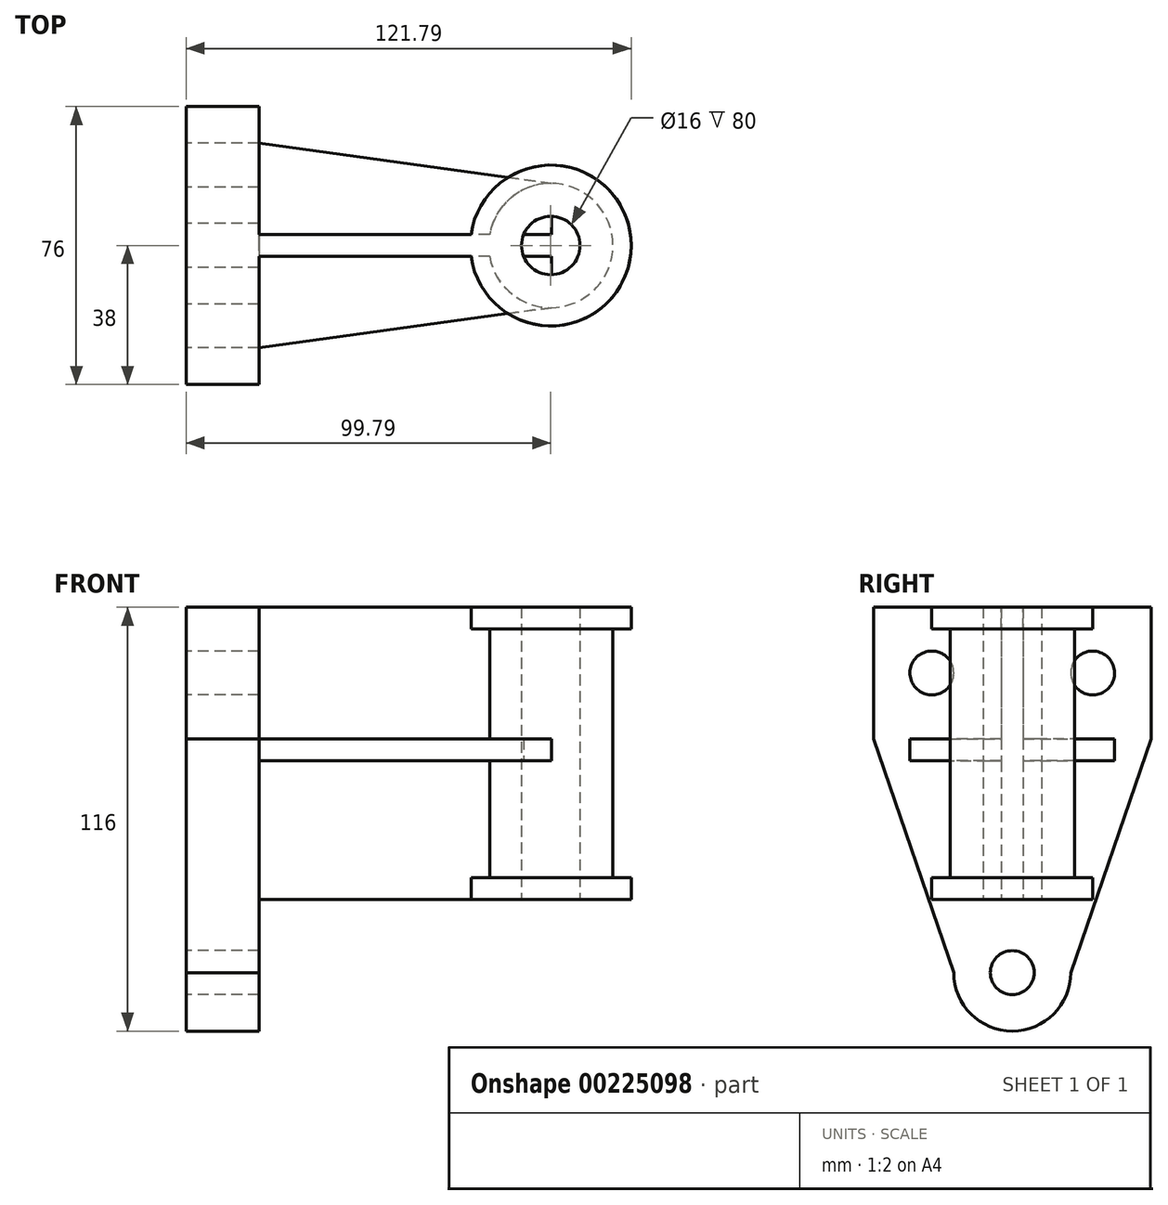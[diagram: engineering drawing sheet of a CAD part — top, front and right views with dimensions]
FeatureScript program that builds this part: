
annotation { "Feature Type Name" : "Feature", "Feature Type Description" : "" }
export const myFeature = defineFeature(function(context is Context, id is Id, definition is map)
    precondition{}
    {
        {
            var Q0;
            Q0=qCreatedBy(makeId("Top.planeOp"),FACE);
            var sketch = newSketch(context, id + "F0", { "sketchPlane" : qUnion([Q0])});
            skCircle(sketch, "E0", {"center": v(0, 0) * mm, "radius": 22 * mm});
            skCircle(sketch, "E1", {"center": v(0, 0) * mm, "radius": 17 * mm});
            skCircle(sketch, "E2", {"center": v(0, 0) * mm, "radius": 8 * mm});
            skSolve(sketch);
        }
        {
            var Q0;
            Q0=makeQuery(id+"F0.imprint","IMPRINT",FACE,{"disambiguationData":[TD([[makeQuery(id+"F0.imprint","IMPRINT",EDGE,{"derivedFrom":sQuery(id+"F0.wireOp",EDGE,"E0")}),1.0]])]});
            extrude(context, id + "F1", {"entities" : qUnion([Q0]), "depth" : 6 * mm});
        }
        {
            var Q0;
            Q0=makeQuery(id+"F0.imprint","IMPRINT",FACE,{"disambiguationData":[TD([[makeQuery(id+"F0.imprint","IMPRINT",EDGE,{"derivedFrom":sQuery(id+"F0.wireOp",EDGE,"E1")}),1.0]])]});
            extrude(context, id + "F2", {"entities" : qUnion([Q0]), "operationType" : NewBodyOperationType.ADD, "depth" : 40 * mm});
        }
        {
            var Q0;
            Q0=makeQuery(id+"F1.opExtrude","SWEPT_BODY",BODY,{"disambiguationData":[OSD([sQuery(id+"F0.wireOp",EDGE,"E0"),sQuery(id+"F0.wireOp",EDGE,"E1")])]});
            var Q1;
            Q1=makeQuery(id+"F2.opExtrude","CAP_FACE",FACE,{"disambiguationData":[OSD([sQuery(id+"F0.wireOp",EDGE,"E1"),sQuery(id+"F0.wireOp",EDGE,"E2")])],"isStart":false});
            mirror(context, id + "F3", {"entities" : qUnion([Q0]), "mirrorPlane" : qUnion([Q1])});
        }
        {
            var Q0;
            Q0=qCreatedBy(makeId("Top.planeOp"),FACE);
            var sketch = newSketch(context, id + "F4", { "sketchPlane" : qUnion([Q0])});
            skLineSegment(sketch, "E3", {"start": v(37.48, 0) * mm, "end": v(-105.07, 0) * mm, "construction": true});
            skLineSegment(sketch, "E4", {"start": v(-21.8, 3) * mm, "end": v(-99.8, 3) * mm});
            skLineSegment(sketch, "E5", {"start": v(-99.8, 3) * mm, "end": v(-99.8, -3) * mm});
            skLineSegment(sketch, "E6", {"start": v(-99.8, -3) * mm, "end": v(-21.8, -3) * mm});
            skLineSegment(sketch, "E7", {"start": v(-21.8, 3) * mm, "end": v(-16.73, 3) * mm});
            skLineSegment(sketch, "E8", {"start": v(-16.73, 3) * mm, "end": v(-16.73, -3) * mm});
            skLineSegment(sketch, "E9", {"start": v(-16.73, -3) * mm, "end": v(-21.8, -3) * mm});
            skSolve(sketch);
        }
        {
            var Q0;
            Q0=makeQuery(id+"F1.opExtrude","SWEPT_BODY",BODY,{"disambiguationData":[OSD([sQuery(id+"F0.wireOp",EDGE,"E0"),sQuery(id+"F0.wireOp",EDGE,"E1")])]});
            var Q1;
            Q1=makeQuery(id+"F3.opPattern","COPY",BODY,{"derivedFrom":makeQuery(id+"F1.opExtrude","SWEPT_BODY",BODY,{"disambiguationData":[OSD([sQuery(id+"F0.wireOp",EDGE,"E0"),sQuery(id+"F0.wireOp",EDGE,"E1")])]}),"instanceName":"1"});
            booleanBodies(context, id + "F5", {"operationType" : BooleanOperationType.UNION, "tools" : qUnion([Q0, Q1])});
        }
        {
            var Q0;
            Q0=makeQuery(id+"F4.imprint","IMPRINT",FACE,{"disambiguationData":[TD([[makeQuery(id+"F4.imprint","IMPRINT",EDGE,{"derivedFrom":sQuery(id+"F4.wireOp",EDGE,"E4")}),1.0]])]});
            var Q1;
            {var subQ0=sQuery(id+"F0.wireOp",EDGE,"E1");Q1=makeQuery(id+"F3.opPattern","COPY",FACE,{"derivedFrom":makeQuery(id+"F2.boolean.opBoolean","MERGE",FACE,{"derivedFrom":[makeQuery(id+"F1.opExtrude","CAP_FACE",FACE,{"disambiguationData":[OSD([sQuery(id+"F0.wireOp",EDGE,"E0"),subQ0])],"isStart":true}),makeQuery(id+"F2.opExtrude","CAP_FACE",FACE,{"disambiguationData":[OSD([subQ0,sQuery(id+"F0.wireOp",EDGE,"E2")])],"isStart":true})]}),"instanceName":"1"});}
            extrude(context, id + "F6", {"entities" : qUnion([Q0]), "operationType" : NewBodyOperationType.ADD, "endBound" : BoundingType.UP_TO_SURFACE, "endBoundEntityFace" : qUnion([Q1]), "depth" : 25 * mm});
        }
        {
            var Q0;
            Q0=makeQuery(id+"F6.opExtrude","SWEPT_FACE",FACE,{"disambiguationData":[OSD([sQuery(id+"F4.wireOp",EDGE,"E5")])]});
            var sketch = newSketch(context, id + "F7", { "sketchPlane" : qUnion([Q0])});
            skLineSegment(sketch, "E10", {"start": v(0, 102.74) * mm, "end": v(0, -20) * mm, "construction": true});
            skLineSegment(sketch, "E11", {"start": v(0, 80) * mm, "end": v(38, 80) * mm});
            skPoint(sketch, "E11.endSnap0", {"position": v(0, 80) * mm});
            skLineSegment(sketch, "E12", {"start": v(38, 80) * mm, "end": v(38, 44) * mm});
            skLineSegment(sketch, "E13", {"start": v(0, 80) * mm, "end": v(-38, 80) * mm});
            skLineSegment(sketch, "E14", {"start": v(-38, 80) * mm, "end": v(-38, 44) * mm});
            skLineSegment(sketch, "E15", {"start": v(-56.56, 62) * mm, "end": v(67.41, 62) * mm, "construction": true});
            skLineSegment(sketch, "E16", {"start": v(-84.06, -20) * mm, "end": v(98, -20) * mm, "construction": true});
            skCircle(sketch, "E17", {"center": v(0, -20) * mm, "radius": 6 * mm});
            skArc(sketch, "E18", {"start": v(-16, -20) * mm, "mid": v(0, -36) * mm, "end": v(16, -20) * mm});
            skLineSegment(sketch, "E19", {"start": v(-16, -20) * mm, "end": v(-38, 44) * mm});
            skLineSegment(sketch, "E20", {"start": v(16, -20) * mm, "end": v(38, 44) * mm});
            skCircle(sketch, "E21", {"center": v(-22, 62) * mm, "radius": 6 * mm});
            skCircle(sketch, "E22", {"center": v(22, 62) * mm, "radius": 6 * mm});
            skLineSegment(sketch, "E23", {"start": v(-28, 44) * mm, "end": v(28, 44) * mm});
            skLineSegment(sketch, "E24", {"start": v(28, 44) * mm, "end": v(28, 38) * mm});
            skLineSegment(sketch, "E25", {"start": v(28, 38) * mm, "end": v(-28, 38) * mm});
            skLineSegment(sketch, "E26", {"start": v(-28, 38) * mm, "end": v(-28, 44) * mm});
            skSolve(sketch);
        }
        {
            var Q0;
            {var subQ9=sQuery(id+"F7.wireOp",EDGE,"E12");Q0=makeQuery(id+"F7.imprint","IMPRINT",FACE,{"disambiguationData":[TD([[makeQuery(id+"F7.imprint","IMPRINT",EDGE,{"derivedFrom":subQ9}),-1.0]])]});}
            extrude(context, id + "F8", {"entities" : qUnion([Q0]), "operationType" : NewBodyOperationType.ADD, "oppositeDirection" : true, "depth" : 20 * mm});
        }
        {
            var Q0;
            {var subQ0=sQuery(id+"F4.wireOp",EDGE,"E5");Q0=makeQuery(id+"F8.boolean.opBoolean","MERGE",FACE,{"derivedFrom":[makeQuery(id+"F6.opExtrude","SWEPT_FACE",FACE,{"disambiguationData":[OSD([subQ0])]}),makeQuery(id+"F8.opExtrude","CAP_FACE",FACE,{"disambiguationData":[OSD([sQuery(id+"F4.wireOp",EDGE,"E4"),subQ0,sQuery(id+"F4.wireOp",EDGE,"E6"),sQuery(id+"F7.wireOp",EDGE,"E11"),sQuery(id+"F7.wireOp",EDGE,"E12"),sQuery(id+"F7.wireOp",EDGE,"E13"),sQuery(id+"F7.wireOp",EDGE,"E14"),sQuery(id+"F7.wireOp",EDGE,"E17"),sQuery(id+"F7.wireOp",EDGE,"E18"),sQuery(id+"F7.wireOp",EDGE,"E19"),sQuery(id+"F7.wireOp",EDGE,"E20"),sQuery(id+"F7.wireOp",EDGE,"E21"),sQuery(id+"F7.wireOp",EDGE,"E22")])],"isStart":true})]});}
            var sketch = newSketch(context, id + "F9", { "sketchPlane" : qUnion([Q0])});
            skSolve(sketch);
        }
        {
            var Q0;
            {var subQ0=sQuery(id+"F7.wireOp",EDGE,"E26");Q0=makeQuery(id+"F9.imprint","IMPRINT",FACE,{"disambiguationData":[TD([[makeQuery(id+"F9.imprint","IMPRINT",EDGE,{"derivedFrom":makeQuery(id+"F8.opExtrude","CAP_EDGE",EDGE,{"disambiguationData":[OSD([subQ0])],"isStart":true})}),-1.0]])]});}
            var Q1;
            {var subQ0=sQuery(id+"F7.wireOp",EDGE,"E24");Q1=makeQuery(id+"F9.imprint","IMPRINT",FACE,{"disambiguationData":[TD([[makeQuery(id+"F9.imprint","IMPRINT",EDGE,{"derivedFrom":makeQuery(id+"F8.opExtrude","CAP_EDGE",EDGE,{"disambiguationData":[OSD([subQ0])],"isStart":true})}),-1.0]])]});}
            extrude(context, id + "F10", {"entities" : qUnion([Q0, Q1]), "operationType" : NewBodyOperationType.ADD, "oppositeDirection" : true, "depth" : 100 * mm});
        }
        {
            var Q0;
            {var subQ2=sQuery(id+"F7.wireOp",EDGE,"E24");var subQ3=sQuery(id+"F7.wireOp",EDGE,"E23");var subQ5=makeQuery(id+"F2.opExtrude","SWEPT_FACE",FACE,{"disambiguationData":[OSD([sQuery(id+"F0.wireOp",EDGE,"E1")])]});Q0=makeQuery(id+"F10.boolean.opBoolean","SPLIT",FACE,{"disambiguationData":[TD([subQ5])],"derivedFrom":makeQuery(id+"F10.opExtrude","SWEPT_FACE",FACE,{"disambiguationData":[OSD([subQ3]),TDD([makeQuery(id+"F9.imprint","IMPRINT",EDGE,{"derivedFrom":makeQuery(id+"F8.opExtrude","CAP_EDGE",EDGE,{"disambiguationData":[OSD([subQ3]),TDD([makeQuery(id+"F7.imprint","IMPRINT",EDGE,{"disambiguationData":[TD([[makeQuery(id+"F7.imprint","INTERSECT",VERTEX,{"derivedFrom":[subQ3,subQ2]}),1.0]])],"derivedFrom":subQ3})])],"isStart":true})})])]})});}
            var sketch = newSketch(context, id + "F11", { "sketchPlane" : qUnion([Q0])});
            skLineSegment(sketch, "E27", {"start": v(-79.8, -28) * mm, "end": v(0.2, -17) * mm});
            skLineSegment(sketch, "E28", {"start": v(0.2, -17) * mm, "end": v(0.2, -28) * mm});
            skLineSegment(sketch, "E29", {"start": v(0.2, -28) * mm, "end": v(-79.8, -28) * mm});
            skSolve(sketch);
        }
        {
            var Q0;
            Q0=makeQuery(id+"F11.imprint","IMPRINT",FACE,{"disambiguationData":[TD([[makeQuery(id+"F11.imprint","IMPRINT",EDGE,{"derivedFrom":sQuery(id+"F11.wireOp",EDGE,"E27")}),-1.0]])]});
            extrude(context, id + "F12", {"entities" : qUnion([Q0]), "operationType" : NewBodyOperationType.REMOVE, "endBound" : BoundingType.UP_TO_NEXT, "oppositeDirection" : true, "depth" : 25 * mm});
        }
        {
            var Q0;
            {var subQ1=sQuery(id+"F7.wireOp",EDGE,"E26");var subQ3=sQuery(id+"F7.wireOp",EDGE,"E23");var subQ5=makeQuery(id+"F2.opExtrude","SWEPT_FACE",FACE,{"disambiguationData":[OSD([sQuery(id+"F0.wireOp",EDGE,"E1")])]});Q0=makeQuery(id+"F10.boolean.opBoolean","SPLIT",FACE,{"disambiguationData":[TD([subQ5])],"derivedFrom":makeQuery(id+"F10.opExtrude","SWEPT_FACE",FACE,{"disambiguationData":[OSD([subQ3]),TDD([makeQuery(id+"F9.imprint","IMPRINT",EDGE,{"derivedFrom":makeQuery(id+"F8.opExtrude","CAP_EDGE",EDGE,{"disambiguationData":[OSD([subQ3]),TDD([makeQuery(id+"F7.imprint","IMPRINT",EDGE,{"disambiguationData":[TD([[makeQuery(id+"F7.imprint","INTERSECT",VERTEX,{"derivedFrom":[subQ3,subQ1]}),-1.0]])],"derivedFrom":subQ3})])],"isStart":true})})])]})});}
            var sketch = newSketch(context, id + "F13", { "sketchPlane" : qUnion([Q0])});
            skLineSegment(sketch, "E30", {"start": v(-79.8, 28) * mm, "end": v(0.2, 17) * mm});
            skLineSegment(sketch, "E31", {"start": v(0.2, 17) * mm, "end": v(0.2, 28) * mm});
            skLineSegment(sketch, "E32", {"start": v(0.2, 28) * mm, "end": v(-79.8, 28) * mm});
            skSolve(sketch);
        }
        {
            var Q0;
            Q0=makeQuery(id+"F13.imprint","IMPRINT",FACE,{"disambiguationData":[TD([[makeQuery(id+"F13.imprint","IMPRINT",EDGE,{"derivedFrom":sQuery(id+"F13.wireOp",EDGE,"E30")}),1.0]])]});
            extrude(context, id + "F14", {"entities" : qUnion([Q0]), "operationType" : NewBodyOperationType.REMOVE, "endBound" : BoundingType.UP_TO_NEXT, "oppositeDirection" : true, "depth" : 25 * mm});
        }
    });
